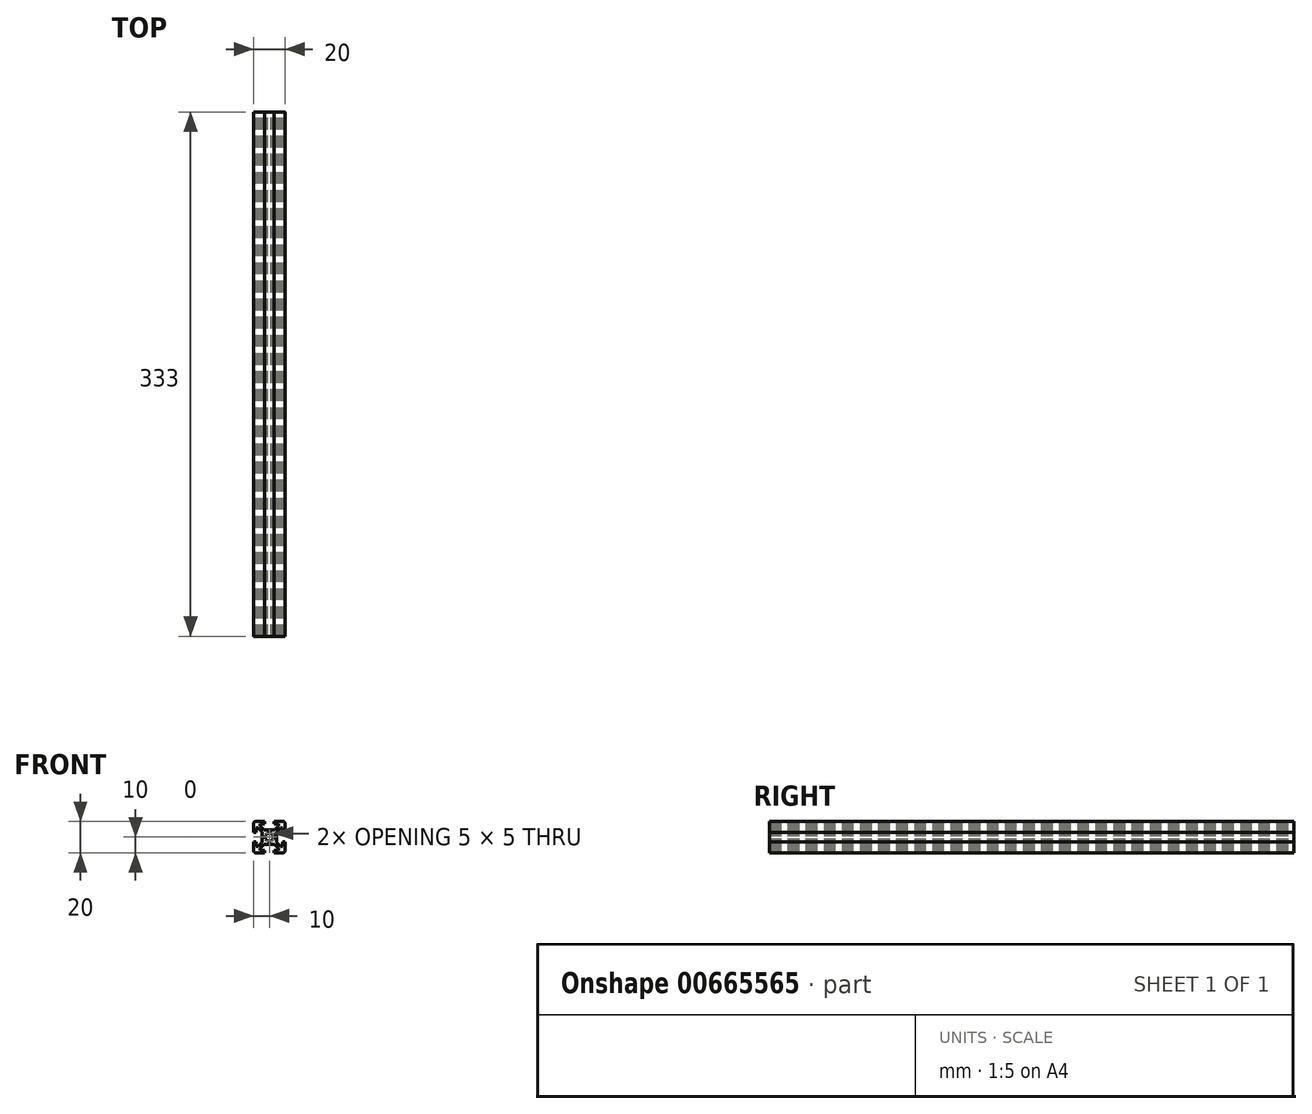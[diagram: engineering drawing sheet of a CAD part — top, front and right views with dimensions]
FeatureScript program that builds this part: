
annotation { "Feature Type Name" : "Feature", "Feature Type Description" : "" }
export const myFeature = defineFeature(function(context is Context, id is Id, definition is map)
    precondition{}
    {
        {
            var Q0;
            Q0=qCreatedBy(makeId("Front.planeOp"),FACE);
            var sketch = newSketch(context, id + "F0", { "sketchPlane" : qUnion([Q0])});
            skLineSegment(sketch, "E0.bottom", {"start": v(8.5, -10) * mm, "end": v(3, -10) * mm});
            skLineSegment(sketch, "E0.top", {"start": v(8.5, 10) * mm, "end": v(3, 10) * mm});
            skLineSegment(sketch, "E0.left", {"start": v(10, -8.5) * mm, "end": v(10, -3) * mm});
            skLineSegment(sketch, "E0.right", {"start": v(-10, -8.5) * mm, "end": v(-10, -3) * mm});
            skPoint(sketch, "E0.middle", {"position": v(0, 0) * mm});
            skLineSegment(sketch, "E1.bottom", {"start": v(6, -8.5) * mm, "end": v(3, -8.5) * mm});
            skLineSegment(sketch, "E1.top", {"start": v(6, 8.5) * mm, "end": v(3, 8.5) * mm});
            skLineSegment(sketch, "E1.left", {"start": v(8.5, -6) * mm, "end": v(8.5, -3) * mm});
            skLineSegment(sketch, "E1.right", {"start": v(-8.5, -6) * mm, "end": v(-8.5, -3) * mm});
            skLineSegment(sketch, "E2.bottom", {"start": v(3.44, -4.5) * mm, "end": v(-3.44, -4.5) * mm});
            skLineSegment(sketch, "E2.top", {"start": v(3.44, 4.5) * mm, "end": v(-3.44, 4.5) * mm});
            skLineSegment(sketch, "E2.left", {"start": v(4.5, -3.44) * mm, "end": v(4.5, 3.44) * mm});
            skLineSegment(sketch, "E2.right", {"start": v(-4.5, -3.44) * mm, "end": v(-4.5, 3.44) * mm});
            skLineSegment(sketch, "E3.bottom", {"start": v(8.5, -6) * mm, "end": v(7.06, -6) * mm});
            skLineSegment(sketch, "E3.top", {"start": v(8.5, 6) * mm, "end": v(7.06, 6) * mm});
            skLineSegment(sketch, "E4.left", {"start": v(6, -8.5) * mm, "end": v(6, -7.06) * mm});
            skLineSegment(sketch, "E4.right", {"start": v(-6, -8.5) * mm, "end": v(-6, -7.06) * mm});
            skPoint(sketch, "E5.orphan", {"position": v(-8.5, 8.5) * mm});
            skPoint(sketch, "E6.orphan", {"position": v(8.5, 8.5) * mm});
            skPoint(sketch, "E7.orphan", {"position": v(8.5, -8.5) * mm});
            skPoint(sketch, "E8.orphan", {"position": v(-8.5, -8.5) * mm});
            skLineSegment(sketch, "E9.trimOffspring", {"start": v(-6, 7.06) * mm, "end": v(-6, 8.5) * mm});
            skLineSegment(sketch, "E10.trimOffspring", {"start": v(-7.06, 6) * mm, "end": v(-8.5, 6) * mm});
            skLineSegment(sketch, "E11.trimOffspring", {"start": v(6, 7.06) * mm, "end": v(6, 8.5) * mm});
            skLineSegment(sketch, "E12.trimOffspring", {"start": v(-7.06, -6) * mm, "end": v(-8.5, -6) * mm});
            skLineSegment(sketch, "E13", {"start": v(-10, 10) * mm, "end": v(0, 0) * mm, "construction": true});
            skLineSegment(sketch, "E14", {"start": v(10, 10) * mm, "end": v(0, 0) * mm, "construction": true});
            skLineSegment(sketch, "E15", {"start": v(-6, 7.06) * mm, "end": v(-3.44, 4.5) * mm});
            skPoint(sketch, "E15.endSnap0", {"position": v(7.25, -6) * mm});
            skLineSegment(sketch, "E16", {"start": v(6, -7.06) * mm, "end": v(3.44, -4.5) * mm});
            skLineSegment(sketch, "E17", {"start": v(7.06, 6) * mm, "end": v(4.5, 3.44) * mm});
            skLineSegment(sketch, "E18", {"start": v(6, 7.06) * mm, "end": v(3.44, 4.5) * mm});
            skPoint(sketch, "E19.orphan", {"position": v(6, -6) * mm});
            skPoint(sketch, "E20.orphan", {"position": v(-4.5, -4.5) * mm});
            skPoint(sketch, "E21.orphan", {"position": v(-4.5, 4.5) * mm});
            skPoint(sketch, "E22.orphan", {"position": v(4.5, 4.5) * mm});
            skPoint(sketch, "E23.orphan", {"position": v(4.5, -4.5) * mm});
            skLineSegment(sketch, "E24.trimOffspring", {"start": v(4.5, -3.44) * mm, "end": v(7.06, -6) * mm});
            skLineSegment(sketch, "E25.trimOffspring", {"start": v(-3.44, -4.5) * mm, "end": v(-6, -7.06) * mm});
            skLineSegment(sketch, "E26.trimOffspring", {"start": v(-4.5, -3.44) * mm, "end": v(-7.06, -6) * mm});
            skLineSegment(sketch, "E27.trimOffspring", {"start": v(-4.5, 3.44) * mm, "end": v(-7.06, 6) * mm});
            skLineSegment(sketch, "E28.bottom", {"start": v(8.5, -3) * mm, "end": v(10, -3) * mm});
            skLineSegment(sketch, "E28.top", {"start": v(8.5, 3) * mm, "end": v(10, 3) * mm});
            skPoint(sketch, "E28.middle", {"position": v(10, 0) * mm});
            skLineSegment(sketch, "E29.left", {"start": v(3, 8.5) * mm, "end": v(3, 10) * mm});
            skLineSegment(sketch, "E29.right", {"start": v(-3, 8.5) * mm, "end": v(-3, 10) * mm});
            skPoint(sketch, "E29.middle", {"position": v(0, 10) * mm});
            skLineSegment(sketch, "E30.bottom", {"start": v(-8.5, 3) * mm, "end": v(-10, 3) * mm});
            skLineSegment(sketch, "E30.top", {"start": v(-8.5, -3) * mm, "end": v(-10, -3) * mm});
            skPoint(sketch, "E30.middle", {"position": v(-10, 0) * mm});
            skLineSegment(sketch, "E31.left", {"start": v(3, -8.5) * mm, "end": v(3, -10) * mm});
            skLineSegment(sketch, "E31.right", {"start": v(-3, -8.5) * mm, "end": v(-3, -10) * mm});
            skPoint(sketch, "E31.middle", {"position": v(0, -10) * mm});
            skPoint(sketch, "E32.orphan", {"position": v(3, 11.5) * mm});
            skPoint(sketch, "E33.orphan", {"position": v(-3, 11.5) * mm});
            skLineSegment(sketch, "E34.trimOffspring", {"start": v(-3, 10) * mm, "end": v(-8.5, 10) * mm});
            skLineSegment(sketch, "E35.trimOffspring", {"start": v(-3, 8.5) * mm, "end": v(-6, 8.5) * mm});
            skPoint(sketch, "E28.right.end.orphan", {"position": v(11.5, 3) * mm});
            skPoint(sketch, "E36.orphan", {"position": v(11.5, -3) * mm});
            skLineSegment(sketch, "E37.trimOffspring", {"start": v(10, 3) * mm, "end": v(10, 8.5) * mm});
            skLineSegment(sketch, "E38.trimOffspring", {"start": v(8.5, 3) * mm, "end": v(8.5, 6) * mm});
            skPoint(sketch, "E39.orphan", {"position": v(3, -11.5) * mm});
            skPoint(sketch, "E40.orphan", {"position": v(-3, -11.5) * mm});
            skLineSegment(sketch, "E41.trimOffspring", {"start": v(-3, -10) * mm, "end": v(-8.5, -10) * mm});
            skLineSegment(sketch, "E42.trimOffspring", {"start": v(-3, -8.5) * mm, "end": v(-6, -8.5) * mm});
            skPoint(sketch, "E30.right.end.orphan", {"position": v(-11.5, -3) * mm});
            skPoint(sketch, "E43.orphan", {"position": v(-11.5, 3) * mm});
            skLineSegment(sketch, "E44.trimOffspring", {"start": v(-10, 3) * mm, "end": v(-10, 8.5) * mm});
            skLineSegment(sketch, "E45.trimOffspring", {"start": v(-8.5, 3) * mm, "end": v(-8.5, 6) * mm});
            skLineSegment(sketch, "E46.trimOffspring", {"start": v(0, 0) * mm, "end": v(10, -10) * mm, "construction": true});
            skLineSegment(sketch, "E47.trimOffspring", {"start": v(0, 0) * mm, "end": v(-10, -10) * mm, "construction": true});
            skArc(sketch, "E48", {"start": v(1.16, 2.22) * mm, "mid": v(0, 2.5) * mm, "end": v(-1.16, 2.22) * mm});
            skLineSegment(sketch, "E49", {"start": v(-2.5, -1.44) * mm, "end": v(1.44, 2.5) * mm});
            skLineSegment(sketch, "E50", {"start": v(2.5, 1.44) * mm, "end": v(-1.44, -2.5) * mm});
            skLineSegment(sketch, "E51", {"start": v(1.44, -2.5) * mm, "end": v(-2.5, 1.44) * mm});
            skLineSegment(sketch, "E52", {"start": v(-1.44, 2.5) * mm, "end": v(2.5, -1.44) * mm});
            skLineSegment(sketch, "E53", {"start": v(2.5, 1.44) * mm, "end": v(2.5, -1.44) * mm, "construction": true});
            skLineSegment(sketch, "E54", {"start": v(1.44, -2.5) * mm, "end": v(-1.44, -2.5) * mm, "construction": true});
            skLineSegment(sketch, "E55", {"start": v(-2.5, -1.44) * mm, "end": v(-2.5, 1.44) * mm, "construction": true});
            skLineSegment(sketch, "E56", {"start": v(-1.44, 2.5) * mm, "end": v(1.44, 2.5) * mm, "construction": true});
            skLineSegment(sketch, "E57", {"start": v(-1.44, 2.5) * mm, "end": v(-2.5, 1.44) * mm});
            skLineSegment(sketch, "E58", {"start": v(1.44, 2.5) * mm, "end": v(2.5, 1.44) * mm});
            skLineSegment(sketch, "E59", {"start": v(2.5, -1.44) * mm, "end": v(1.44, -2.5) * mm});
            skLineSegment(sketch, "E60", {"start": v(-1.44, -2.5) * mm, "end": v(-2.5, -1.44) * mm});
            skArc(sketch, "E61.trimOffspring", {"start": v(-2.22, 1.16) * mm, "mid": v(-2.5, 0) * mm, "end": v(-2.22, -1.16) * mm});
            skArc(sketch, "E62.trimOffspring", {"start": v(-1.16, -2.22) * mm, "mid": v(0, -2.5) * mm, "end": v(1.16, -2.22) * mm});
            skArc(sketch, "E63.trimOffspring", {"start": v(2.22, -1.16) * mm, "mid": v(2.5, 0) * mm, "end": v(2.22, 1.16) * mm});
            skPoint(sketch, "E64.visualSharp", {"position": v(10, 10) * mm});
            skArc(sketch, "E64.filletArc", {"start": v(10, 8.5) * mm, "mid": v(9.56, 9.56) * mm, "end": v(8.5, 10) * mm});
            skPoint(sketch, "E65.visualSharp", {"position": v(10, -10) * mm});
            skArc(sketch, "E65.filletArc", {"start": v(8.5, -10) * mm, "mid": v(9.56, -9.56) * mm, "end": v(10, -8.5) * mm});
            skPoint(sketch, "E66.visualSharp", {"position": v(-10, -10) * mm});
            skArc(sketch, "E66.filletArc", {"start": v(-10, -8.5) * mm, "mid": v(-9.56, -9.56) * mm, "end": v(-8.5, -10) * mm});
            skPoint(sketch, "E67.visualSharp", {"position": v(-10, 10) * mm});
            skArc(sketch, "E67.filletArc", {"start": v(-8.5, 10) * mm, "mid": v(-9.56, 9.56) * mm, "end": v(-10, 8.5) * mm});
            skSolve(sketch);
        }
        {
            assignVariable(context, id + "F2", {"name" : "Length", "anyValue" : 333});
        }
        {
            var Q0;
            Q0=qSketchRegion(id+"F0",true);
            extrude(context, id + "F1", {"entities" : qUnion([Q0]), "depth" : (getVariable(context, 'Length')) * mm});
        }
    });
